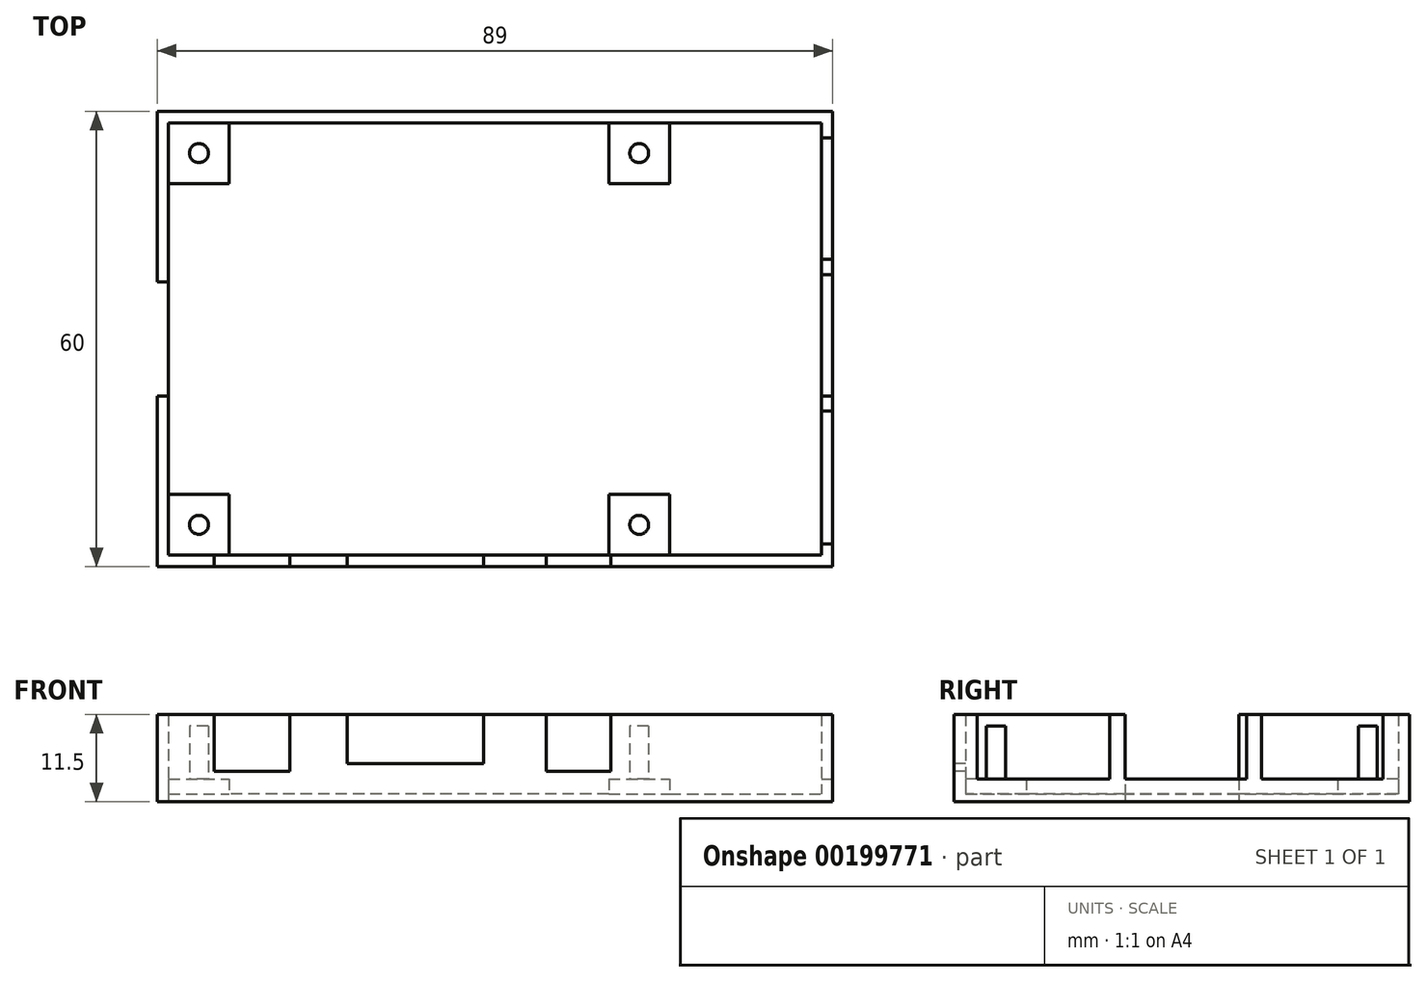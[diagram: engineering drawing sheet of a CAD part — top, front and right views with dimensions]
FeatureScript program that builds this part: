
annotation { "Feature Type Name" : "Feature", "Feature Type Description" : "" }
export const myFeature = defineFeature(function(context is Context, id is Id, definition is map)
    precondition{}
    {
        {
            var Q0;
            Q0=qCreatedBy(makeId("Top.planeOp"),FACE);
            var sketch = newSketch(context, id + "F0", { "sketchPlane" : qUnion([Q0])});
            skLineSegment(sketch, "E0.bottom", {"start": v(0, 0) * mm, "end": v(89, 0) * mm});
            skLineSegment(sketch, "E0.top", {"start": v(0, 60) * mm, "end": v(89, 60) * mm});
            skLineSegment(sketch, "E0.left", {"start": v(0, 0) * mm, "end": v(0, 60) * mm});
            skLineSegment(sketch, "E0.right", {"start": v(89, 0) * mm, "end": v(89, 60) * mm});
            skSolve(sketch);
        }
        {
            var Q0;
            Q0=makeQuery(id+"F0.imprint","IMPRINT",FACE,{"disambiguationData":[TD([[makeQuery(id+"F0.imprint","IMPRINT",EDGE,{"derivedFrom":sQuery(id+"F0.wireOp",EDGE,"E0.bottom")}),1.0]])]});
            extrude(context, id + "F1", {"entities" : qUnion([Q0]), "depth" : 1 * mm});
        }
        {
            var Q0;
            Q0=makeQuery(id+"F1.opExtrude","CAP_FACE",FACE,{"disambiguationData":[OSD([sQuery(id+"F0.wireOp",EDGE,"E0.bottom"),sQuery(id+"F0.wireOp",EDGE,"E0.top"),sQuery(id+"F0.wireOp",EDGE,"E0.left"),sQuery(id+"F0.wireOp",EDGE,"E0.right")])],"isStart":false});
            var sketch = newSketch(context, id + "F2", { "sketchPlane" : qUnion([Q0])});
            skLineSegment(sketch, "E1.0", {"start": v(1.5, 58.5) * mm, "end": v(1.5, 1.5) * mm});
            skLineSegment(sketch, "E1.1", {"start": v(87.5, 58.5) * mm, "end": v(1.5, 58.5) * mm});
            skLineSegment(sketch, "E1.2", {"start": v(87.5, 1.5) * mm, "end": v(87.5, 58.5) * mm});
            skLineSegment(sketch, "E1.3", {"start": v(1.5, 1.5) * mm, "end": v(87.5, 1.5) * mm});
            skSolve(sketch);
        }
        {
            var Q0;
            Q0=makeQuery(id+"F2.imprint","IMPRINT",FACE,{"disambiguationData":[TD([[makeQuery(id+"F2.imprint","IMPRINT",EDGE,{"derivedFrom":sQuery(id+"F2.wireOp",EDGE,"E1.0")}),-1.0]])]});
            extrude(context, id + "F3", {"entities" : qUnion([Q0]), "operationType" : NewBodyOperationType.ADD, "depth" : 10.5 * mm});
        }
        {
            var Q0;
            {var subQ0=sQuery(id+"F0.wireOp",EDGE,"E0.left");Q0=makeQuery(id+"F3.boolean.opBoolean","MERGE",FACE,{"derivedFrom":[makeQuery(id+"F1.opExtrude","SWEPT_FACE",FACE,{"disambiguationData":[OSD([subQ0])]}),makeQuery(id+"F3.opExtrude","SWEPT_FACE",FACE,{"disambiguationData":[OSD([subQ0])]})]});}
            var sketch = newSketch(context, id + "F4", { "sketchPlane" : qUnion([Q0])});
            skLineSegment(sketch, "E2.bottom", {"start": v(-37.5, 11.5) * mm, "end": v(-22.5, 11.5) * mm});
            skLineSegment(sketch, "E2.top", {"start": v(-37.5, 0) * mm, "end": v(-22.5, 0) * mm});
            skLineSegment(sketch, "E2.left", {"start": v(-37.5, 11.5) * mm, "end": v(-37.5, 0) * mm});
            skLineSegment(sketch, "E2.right", {"start": v(-22.5, 11.5) * mm, "end": v(-22.5, 0) * mm});
            skSolve(sketch);
        }
        {
            var Q0;
            Q0=makeQuery(id+"F4.imprint","IMPRINT",FACE,{"disambiguationData":[TD([[makeQuery(id+"F4.imprint","IMPRINT",EDGE,{"derivedFrom":sQuery(id+"F4.wireOp",EDGE,"E2.bottom")}),1.0]])]});
            var Q1;
            Q1=makeQuery(id+"F3.opExtrude","SWEPT_FACE",FACE,{"disambiguationData":[OSD([sQuery(id+"F2.wireOp",EDGE,"E1.0")])]});
            extrude(context, id + "F5", {"entities" : qUnion([Q0]), "operationType" : NewBodyOperationType.REMOVE, "endBound" : BoundingType.UP_TO_SURFACE, "oppositeDirection" : true, "endBoundEntityFace" : qUnion([Q1]), "depth" : 25 * mm});
        }
        {
            var Q0;
            {var subQ0=sQuery(id+"F0.wireOp",EDGE,"E0.bottom");Q0=makeQuery(id+"F3.boolean.opBoolean","MERGE",FACE,{"derivedFrom":[makeQuery(id+"F1.opExtrude","SWEPT_FACE",FACE,{"disambiguationData":[OSD([subQ0])]}),makeQuery(id+"F3.opExtrude","SWEPT_FACE",FACE,{"disambiguationData":[OSD([subQ0])]})]});}
            var sketch = newSketch(context, id + "F6", { "sketchPlane" : qUnion([Q0])});
            skLineSegment(sketch, "E3.bottom", {"start": v(7.5, 11.5) * mm, "end": v(17.5, 11.5) * mm});
            skLineSegment(sketch, "E3.top", {"start": v(7.5, 4) * mm, "end": v(17.5, 4) * mm});
            skLineSegment(sketch, "E3.left", {"start": v(7.5, 11.5) * mm, "end": v(7.5, 4) * mm});
            skLineSegment(sketch, "E3.right", {"start": v(17.5, 11.5) * mm, "end": v(17.5, 4) * mm});
            skLineSegment(sketch, "E4.bottom", {"start": v(25, 11.5) * mm, "end": v(43, 11.5) * mm});
            skLineSegment(sketch, "E4.top", {"start": v(25, 5) * mm, "end": v(43, 5) * mm});
            skLineSegment(sketch, "E4.left", {"start": v(25, 11.5) * mm, "end": v(25, 5) * mm});
            skLineSegment(sketch, "E4.right", {"start": v(43, 11.5) * mm, "end": v(43, 5) * mm});
            skLineSegment(sketch, "E5.bottom", {"start": v(51.25, 11.5) * mm, "end": v(59.75, 11.5) * mm});
            skLineSegment(sketch, "E5.top", {"start": v(51.25, 4) * mm, "end": v(59.75, 4) * mm});
            skLineSegment(sketch, "E5.left", {"start": v(51.25, 11.5) * mm, "end": v(51.25, 4) * mm});
            skLineSegment(sketch, "E5.right", {"start": v(59.75, 11.5) * mm, "end": v(59.75, 4) * mm});
            skSolve(sketch);
        }
        {
            var Q0;
            Q0=makeQuery(id+"F6.imprint","IMPRINT",FACE,{"disambiguationData":[TD([[makeQuery(id+"F6.imprint","IMPRINT",EDGE,{"derivedFrom":sQuery(id+"F6.wireOp",EDGE,"E3.bottom")}),-1.0]])]});
            var Q1;
            Q1=makeQuery(id+"F6.imprint","IMPRINT",FACE,{"disambiguationData":[TD([[makeQuery(id+"F6.imprint","IMPRINT",EDGE,{"derivedFrom":sQuery(id+"F6.wireOp",EDGE,"E4.bottom")}),-1.0]])]});
            var Q2;
            Q2=makeQuery(id+"F6.imprint","IMPRINT",FACE,{"disambiguationData":[TD([[makeQuery(id+"F6.imprint","IMPRINT",EDGE,{"derivedFrom":sQuery(id+"F6.wireOp",EDGE,"E5.bottom")}),-1.0]])]});
            extrude(context, id + "F7", {"entities" : qUnion([Q0, Q1, Q2]), "operationType" : NewBodyOperationType.REMOVE, "endBound" : BoundingType.UP_TO_NEXT, "oppositeDirection" : true, "depth" : 25 * mm});
        }
        {
            var Q0;
            {var subQ0=sQuery(id+"F0.wireOp",EDGE,"E0.right");Q0=makeQuery(id+"F3.boolean.opBoolean","MERGE",FACE,{"derivedFrom":[makeQuery(id+"F1.opExtrude","SWEPT_FACE",FACE,{"disambiguationData":[OSD([subQ0])]}),makeQuery(id+"F3.opExtrude","SWEPT_FACE",FACE,{"disambiguationData":[OSD([subQ0])]})]});}
            var sketch = newSketch(context, id + "F8", { "sketchPlane" : qUnion([Q0])});
            skLineSegment(sketch, "E6.bottom", {"start": v(3, 11.5) * mm, "end": v(20.5, 11.5) * mm});
            skLineSegment(sketch, "E6.top", {"start": v(3, 3) * mm, "end": v(20.5, 3) * mm});
            skLineSegment(sketch, "E6.left", {"start": v(3, 11.5) * mm, "end": v(3, 3) * mm});
            skLineSegment(sketch, "E6.right", {"start": v(20.5, 11.5) * mm, "end": v(20.5, 3) * mm});
            skLineSegment(sketch, "E7.bottom", {"start": v(22.5, 11.5) * mm, "end": v(38.5, 11.5) * mm});
            skLineSegment(sketch, "E7.top", {"start": v(22.5, 3) * mm, "end": v(38.5, 3) * mm});
            skLineSegment(sketch, "E7.left", {"start": v(22.5, 11.5) * mm, "end": v(22.5, 3) * mm});
            skLineSegment(sketch, "E7.right", {"start": v(38.5, 11.5) * mm, "end": v(38.5, 3) * mm});
            skLineSegment(sketch, "E8.bottom", {"start": v(40.5, 11.5) * mm, "end": v(56.5, 11.5) * mm});
            skLineSegment(sketch, "E8.top", {"start": v(40.5, 3) * mm, "end": v(56.5, 3) * mm});
            skLineSegment(sketch, "E8.left", {"start": v(40.5, 11.5) * mm, "end": v(40.5, 3) * mm});
            skLineSegment(sketch, "E8.right", {"start": v(56.5, 11.5) * mm, "end": v(56.5, 3) * mm});
            skSolve(sketch);
        }
        {
            var Q0;
            Q0=makeQuery(id+"F8.imprint","IMPRINT",FACE,{"disambiguationData":[TD([[makeQuery(id+"F8.imprint","IMPRINT",EDGE,{"derivedFrom":sQuery(id+"F8.wireOp",EDGE,"E6.bottom")}),-1.0]])]});
            var Q1;
            Q1=makeQuery(id+"F8.imprint","IMPRINT",FACE,{"disambiguationData":[TD([[makeQuery(id+"F8.imprint","IMPRINT",EDGE,{"derivedFrom":sQuery(id+"F8.wireOp",EDGE,"E7.bottom")}),-1.0]])]});
            var Q2;
            Q2=makeQuery(id+"F8.imprint","IMPRINT",FACE,{"disambiguationData":[TD([[makeQuery(id+"F8.imprint","IMPRINT",EDGE,{"derivedFrom":sQuery(id+"F8.wireOp",EDGE,"E8.bottom")}),-1.0]])]});
            extrude(context, id + "F9", {"entities" : qUnion([Q0, Q1, Q2]), "operationType" : NewBodyOperationType.REMOVE, "endBound" : BoundingType.UP_TO_NEXT, "oppositeDirection" : true, "depth" : 25 * mm});
        }
        {
            var Q0;
            Q0=makeQuery(id+"F1.opExtrude","CAP_FACE",FACE,{"disambiguationData":[OSD([sQuery(id+"F0.wireOp",EDGE,"E0.bottom"),sQuery(id+"F0.wireOp",EDGE,"E0.top"),sQuery(id+"F0.wireOp",EDGE,"E0.left"),sQuery(id+"F0.wireOp",EDGE,"E0.right")])],"isStart":false});
            var sketch = newSketch(context, id + "F10", { "sketchPlane" : qUnion([Q0])});
            skCircle(sketch, "E9", {"center": v(5.5, 54.5) * mm, "radius": 1.25 * mm});
            skCircle(sketch, "E10.0.1.0", {"center": v(5.5, 5.5) * mm, "radius": 1.25 * mm});
            skCircle(sketch, "E10.1.0.0", {"center": v(63.5, 54.5) * mm, "radius": 1.25 * mm});
            skCircle(sketch, "E10.1.1.0", {"center": v(63.5, 5.5) * mm, "radius": 1.25 * mm});
            skLineSegment(sketch, "E10.direction1", {"start": v(5.5, 54.5) * mm, "end": v(63.5, 54.5) * mm, "construction": true});
            skLineSegment(sketch, "E10.direction2", {"start": v(5.5, 54.5) * mm, "end": v(5.5, 5.5) * mm, "construction": true});
            skSolve(sketch);
        }
        {
            var Q0;
            Q0=makeQuery(id+"F10.imprint","IMPRINT",FACE,{"disambiguationData":[TD([[makeQuery(id+"F10.imprint","IMPRINT",EDGE,{"derivedFrom":sQuery(id+"F10.wireOp",EDGE,"E9")}),1.0]])]});
            var Q1;
            Q1=makeQuery(id+"F10.imprint","IMPRINT",FACE,{"disambiguationData":[TD([[makeQuery(id+"F10.imprint","IMPRINT",EDGE,{"derivedFrom":sQuery(id+"F10.wireOp",EDGE,"E10.1.0.0")}),1.0]])]});
            var Q2;
            Q2=makeQuery(id+"F10.imprint","IMPRINT",FACE,{"disambiguationData":[TD([[makeQuery(id+"F10.imprint","IMPRINT",EDGE,{"derivedFrom":sQuery(id+"F10.wireOp",EDGE,"E10.0.1.0")}),1.0]])]});
            var Q3;
            Q3=makeQuery(id+"F10.imprint","IMPRINT",FACE,{"disambiguationData":[TD([[makeQuery(id+"F10.imprint","IMPRINT",EDGE,{"derivedFrom":sQuery(id+"F10.wireOp",EDGE,"E10.1.1.0")}),1.0]])]});
            extrude(context, id + "F11", {"entities" : qUnion([Q0, Q1, Q2, Q3]), "operationType" : NewBodyOperationType.ADD, "depth" : 9 * mm});
        }
        {
            var Q0;
            Q0=makeQuery(id+"F1.opExtrude","CAP_FACE",FACE,{"disambiguationData":[OSD([sQuery(id+"F0.wireOp",EDGE,"E0.bottom"),sQuery(id+"F0.wireOp",EDGE,"E0.top"),sQuery(id+"F0.wireOp",EDGE,"E0.left"),sQuery(id+"F0.wireOp",EDGE,"E0.right")])],"isStart":false});
            var sketch = newSketch(context, id + "F12", { "sketchPlane" : qUnion([Q0])});
            skLineSegment(sketch, "E11.bottom", {"start": v(1.5, 58.5) * mm, "end": v(9.5, 58.5) * mm});
            skLineSegment(sketch, "E11.top", {"start": v(1.5, 50.5) * mm, "end": v(9.5, 50.5) * mm});
            skLineSegment(sketch, "E11.left", {"start": v(1.5, 58.5) * mm, "end": v(1.5, 50.5) * mm});
            skLineSegment(sketch, "E11.right", {"start": v(9.5, 58.5) * mm, "end": v(9.5, 50.5) * mm});
            skLineSegment(sketch, "E12.0.1.0", {"start": v(9.5, 9.5) * mm, "end": v(9.5, 1.5) * mm});
            skLineSegment(sketch, "E12.0.1.1", {"start": v(1.5, 1.5) * mm, "end": v(9.5, 1.5) * mm});
            skLineSegment(sketch, "E12.0.1.2", {"start": v(1.5, 9.5) * mm, "end": v(1.5, 1.5) * mm});
            skLineSegment(sketch, "E12.0.1.3", {"start": v(1.5, 9.5) * mm, "end": v(9.5, 9.5) * mm});
            skLineSegment(sketch, "E12.1.0.0", {"start": v(67.5, 58.5) * mm, "end": v(67.5, 50.5) * mm});
            skLineSegment(sketch, "E12.1.0.1", {"start": v(59.5, 50.5) * mm, "end": v(67.5, 50.5) * mm});
            skLineSegment(sketch, "E12.1.0.2", {"start": v(59.5, 58.5) * mm, "end": v(59.5, 50.5) * mm});
            skLineSegment(sketch, "E12.1.0.3", {"start": v(59.5, 58.5) * mm, "end": v(67.5, 58.5) * mm});
            skLineSegment(sketch, "E12.1.1.0", {"start": v(67.5, 9.5) * mm, "end": v(67.5, 1.5) * mm});
            skLineSegment(sketch, "E12.1.1.1", {"start": v(59.5, 1.5) * mm, "end": v(67.5, 1.5) * mm});
            skLineSegment(sketch, "E12.1.1.2", {"start": v(59.5, 9.5) * mm, "end": v(59.5, 1.5) * mm});
            skLineSegment(sketch, "E12.1.1.3", {"start": v(59.5, 9.5) * mm, "end": v(67.5, 9.5) * mm});
            skLineSegment(sketch, "E12.direction1", {"start": v(9.5, 50.5) * mm, "end": v(67.5, 50.5) * mm, "construction": true});
            skLineSegment(sketch, "E12.direction2", {"start": v(9.5, 50.5) * mm, "end": v(9.5, 1.5) * mm, "construction": true});
            skSolve(sketch);
        }
        {
            var Q0;
            Q0=makeQuery(id+"F12.imprint","IMPRINT",FACE,{"disambiguationData":[TD([[makeQuery(id+"F12.imprint","IMPRINT",EDGE,{"derivedFrom":sQuery(id+"F12.wireOp",EDGE,"E11.bottom")}),1.0]])]});
            var Q1;
            Q1=makeQuery(id+"F12.imprint","IMPRINT",FACE,{"disambiguationData":[TD([[makeQuery(id+"F12.imprint","IMPRINT",EDGE,{"derivedFrom":sQuery(id+"F12.wireOp",EDGE,"E12.1.0.0")}),-1.0]])]});
            var Q2;
            Q2=makeQuery(id+"F12.imprint","IMPRINT",FACE,{"disambiguationData":[TD([[makeQuery(id+"F12.imprint","IMPRINT",EDGE,{"derivedFrom":sQuery(id+"F12.wireOp",EDGE,"E12.1.1.0")}),-1.0]])]});
            var Q3;
            Q3=makeQuery(id+"F12.imprint","IMPRINT",FACE,{"disambiguationData":[TD([[makeQuery(id+"F12.imprint","IMPRINT",EDGE,{"derivedFrom":sQuery(id+"F12.wireOp",EDGE,"E12.0.1.0")}),-1.0]])]});
            extrude(context, id + "F13", {"entities" : qUnion([Q0, Q1, Q2, Q3]), "operationType" : NewBodyOperationType.ADD, "depth" : 2 * mm});
        }
    });
